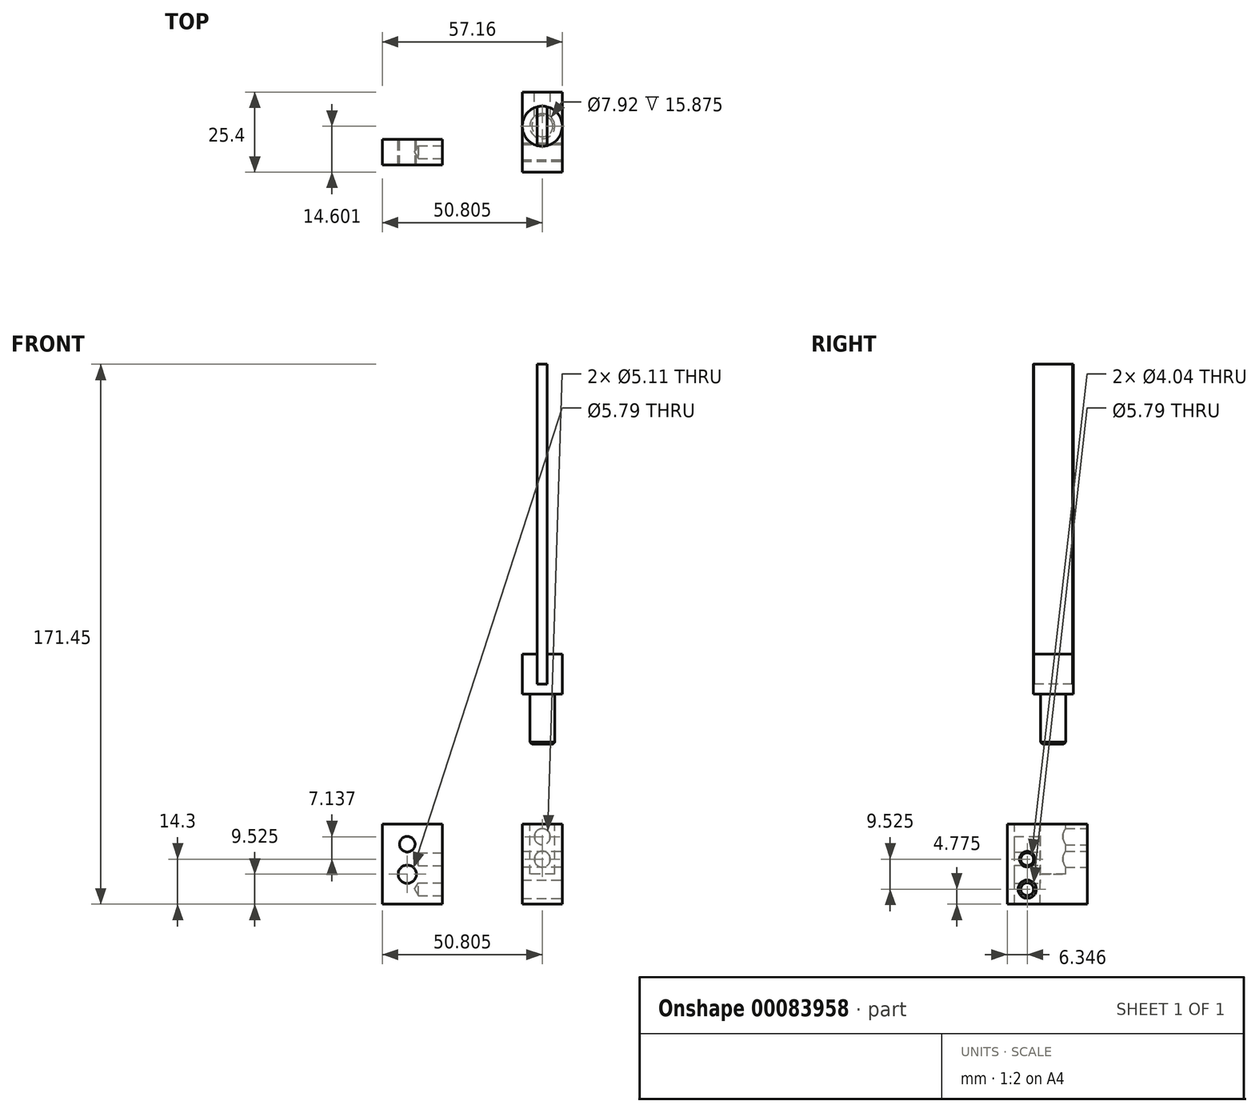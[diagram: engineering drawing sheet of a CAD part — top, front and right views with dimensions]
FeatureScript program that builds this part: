
annotation { "Feature Type Name" : "Feature", "Feature Type Description" : "" }
export const myFeature = defineFeature(function(context is Context, id is Id, definition is map)
    precondition{}
    {
        {
            var Q0;
            Q0=qCreatedBy(makeId("Front.planeOp"),FACE);
            var sketch = newSketch(context, id + "F0", { "sketchPlane" : qUnion([Q0])});
            skLineSegment(sketch, "E0.bottom", {"start": v(-9.52, -12.7) * mm, "end": v(9.53, -12.7) * mm});
            skLineSegment(sketch, "E0.top", {"start": v(-9.53, 12.7) * mm, "end": v(9.53, 12.7) * mm});
            skLineSegment(sketch, "E0.left", {"start": v(-9.53, -12.7) * mm, "end": v(-9.53, 12.7) * mm});
            skLineSegment(sketch, "E0.right", {"start": v(9.53, -12.7) * mm, "end": v(9.53, 12.7) * mm});
            skPoint(sketch, "E0.middle", {"position": v(0, 0) * mm});
            skSolve(sketch);
        }
        {
            var Q0;
            Q0=makeQuery(id+"F0.imprint","IMPRINT",FACE,{"disambiguationData":[TD([[makeQuery(id+"F0.imprint","IMPRINT",EDGE,{"derivedFrom":sQuery(id+"F0.wireOp",EDGE,"E0.bottom")}),1.0]])]});
            extrude(context, id + "F1", {"entities" : qUnion([Q0]), "depth" : 8.13 * mm});
        }
        {
            var Q0;
            Q0=makeQuery(id+"F1.opExtrude","CAP_FACE",FACE,{"disambiguationData":[OSD([sQuery(id+"F0.wireOp",EDGE,"E0.bottom"),sQuery(id+"F0.wireOp",EDGE,"E0.top"),sQuery(id+"F0.wireOp",EDGE,"E0.left"),sQuery(id+"F0.wireOp",EDGE,"E0.right")])],"isStart":true});
            var sketch = newSketch(context, id + "F2", { "sketchPlane" : qUnion([Q0])});
            skLineSegment(sketch, "E1", {"start": v(1.6, 12.7) * mm, "end": v(1.6, -12.7) * mm, "construction": true});
            skLineSegment(sketch, "E2", {"start": v(-9.53, 6.35) * mm, "end": v(9.53, 6.35) * mm, "construction": true});
            skLineSegment(sketch, "E3", {"start": v(-9.53, -3.17) * mm, "end": v(9.53, -3.17) * mm, "construction": true});
            skPoint(sketch, "E4", {"position": v(1.6, 6.35) * mm});
            skPoint(sketch, "E5", {"position": v(1.6, -3.17) * mm});
            skSolve(sketch);
        }
        {
            var Q0;
            Q0=sQuery(id+"F2.wireOp",VERTEX,"E4");
            var Q1;
            Q1=makeQuery(id+"F1.opExtrude","SWEPT_BODY",BODY,{"disambiguationData":[OSD([sQuery(id+"F0.wireOp",EDGE,"E0.bottom"),sQuery(id+"F0.wireOp",EDGE,"E0.top"),sQuery(id+"F0.wireOp",EDGE,"E0.left"),sQuery(id+"F0.wireOp",EDGE,"E0.right")])]});
            hole(context, id + "F3", {"style" : HoleStyle.SIMPLE, "endStyle" : HoleEndStyle.THROUGH, "standardTappedOrClearance" : lookupTablePath({ "standard" : "ANSI", "size" : "#10 (0.2)", "type" : "Drilled" }), "standardBlindInLast" : lookupTablePath({ "standard" : "ANSI", "size" : "#10", "type" : "Drilled" }), "holeDiameter" : 4.9 * mm, "locations" : qUnion([Q0]), "scope" : qUnion([Q1]), "isTappedThrough" : true});
        }
        {
            var Q0;
            Q0=sQuery(id+"F2.wireOp",VERTEX,"E5");
            var Q1;
            Q1=makeQuery(id+"F1.opExtrude","SWEPT_BODY",BODY,{"disambiguationData":[OSD([sQuery(id+"F0.wireOp",EDGE,"E0.bottom"),sQuery(id+"F0.wireOp",EDGE,"E0.top"),sQuery(id+"F0.wireOp",EDGE,"E0.left"),sQuery(id+"F0.wireOp",EDGE,"E0.right")])]});
            hole(context, id + "F4", {"style" : HoleStyle.SIMPLE, "endStyle" : HoleEndStyle.THROUGH, "standardTappedOrClearance" : lookupTablePath({ "standard" : "ANSI", "size" : "#1 (0.23)", "type" : "Drilled" }), "standardBlindInLast" : lookupTablePath({ "standard" : "ANSI", "size" : "#1", "type" : "Drilled" }), "holeDiameter" : 5.8 * mm, "locations" : qUnion([Q0]), "scope" : qUnion([Q1]), "isTappedThrough" : true});
        }
        {
            var Q0;
            Q0=makeQuery(id+"F1.opExtrude","SWEPT_FACE",FACE,{"disambiguationData":[OSD([sQuery(id+"F0.wireOp",EDGE,"E0.right")])]});
            var sketch = newSketch(context, id + "F5", { "sketchPlane" : qUnion([Q0])});
            skLineSegment(sketch, "E6", {"start": v(-4.06, 12.7) * mm, "end": v(-4.06, -12.7) * mm, "construction": true});
            skLineSegment(sketch, "E7", {"start": v(-8.13, 1.6) * mm, "end": v(0, 1.6) * mm, "construction": true});
            skLineSegment(sketch, "E8", {"start": v(-8.13, -7.92) * mm, "end": v(0, -7.92) * mm, "construction": true});
            skPoint(sketch, "E9", {"position": v(-4.06, 1.6) * mm});
            skPoint(sketch, "E10", {"position": v(-4.06, -7.92) * mm});
            skSolve(sketch);
        }
        {
            var Q0;
            Q0=sQuery(id+"F5.wireOp",VERTEX,"E9");
            var Q1;
            Q1=sQuery(id+"F5.wireOp",VERTEX,"E10");
            var Q2;
            Q2=makeQuery(id+"F1.opExtrude","SWEPT_BODY",BODY,{"disambiguationData":[OSD([sQuery(id+"F0.wireOp",EDGE,"E0.bottom"),sQuery(id+"F0.wireOp",EDGE,"E0.top"),sQuery(id+"F0.wireOp",EDGE,"E0.left"),sQuery(id+"F0.wireOp",EDGE,"E0.right")])]});
            hole(context, id + "F6", {"style" : HoleStyle.SIMPLE, "endStyle" : HoleEndStyle.BLIND, "standardTappedOrClearance" : lookupTablePath({ "standard" : "ANSI", "engagement" : "75%", "pitch" : "32 tpi", "size" : "#10", "type" : "Tapped" }), "standardBlindInLast" : lookupTablePath({ "standard" : "ANSI", "engagement" : "75%", "pitch" : "32 tpi", "size" : "#10", "type" : "Tapped" }), "holeDiameter" : 4.04 * mm, "holeDepth" : 7.62 * mm, "locations" : qUnion([Q0, Q1]), "scope" : qUnion([Q2]), "majorDiameter" : 4.83 * mm});
        }
        {
            var Q0;
            Q0=makeQuery(id+"F1.opExtrude","SWEPT_FACE",FACE,{"disambiguationData":[OSD([sQuery(id+"F0.wireOp",EDGE,"E0.right")])]});
            cPlane(context, id + "F7", {"entities" : qUnion([Q0]), "cplaneType" : CPlaneType.OFFSET, "offset" : 25.4 * mm, "width" : 152.4 * mm, "height" : 152.4 * mm});
        }
        {
            var Q0;
            Q0=qCreatedBy(id+"F7.planeOp",FACE);
            var sketch = newSketch(context, id + "F8", { "sketchPlane" : qUnion([Q0])});
            skLineSegment(sketch, "E11.bottom", {"start": v(-10.41, 12.7) * mm, "end": v(14.99, 12.7) * mm});
            skLineSegment(sketch, "E11.top", {"start": v(-10.41, -12.7) * mm, "end": v(14.99, -12.7) * mm});
            skLineSegment(sketch, "E11.left", {"start": v(-10.41, 12.7) * mm, "end": v(-10.41, -12.7) * mm});
            skLineSegment(sketch, "E11.right", {"start": v(14.99, 12.7) * mm, "end": v(14.99, -12.7) * mm});
            skSolve(sketch);
        }
        {
            var Q0;
            Q0=makeQuery(id+"F8.imprint","IMPRINT",FACE,{"disambiguationData":[TD([[makeQuery(id+"F8.imprint","IMPRINT",EDGE,{"derivedFrom":sQuery(id+"F8.wireOp",EDGE,"E11.bottom")}),-1.0]])]});
            extrude(context, id + "F9", {"entities" : qUnion([Q0]), "depth" : 12.7 * mm});
        }
        {
            var Q0;
            Q0=makeQuery(id+"F9.opExtrude","CAP_FACE",FACE,{"disambiguationData":[OSD([sQuery(id+"F8.wireOp",EDGE,"E11.bottom"),sQuery(id+"F8.wireOp",EDGE,"E11.top"),sQuery(id+"F8.wireOp",EDGE,"E11.left"),sQuery(id+"F8.wireOp",EDGE,"E11.right")])],"isStart":false});
            var sketch = newSketch(context, id + "F10", { "sketchPlane" : qUnion([Q0])});
            skPoint(sketch, "E12.0", {"position": v(-4.06, 1.6) * mm});
            skPoint(sketch, "E13.0", {"position": v(-4.06, -7.92) * mm});
            skSolve(sketch);
        }
        {
            var Q0;
            Q0=sQuery(id+"F10.wireOp",VERTEX,"E12.0");
            var Q1;
            Q1=makeQuery(id+"F9.opExtrude","SWEPT_BODY",BODY,{"disambiguationData":[OSD([sQuery(id+"F8.wireOp",EDGE,"E11.bottom"),sQuery(id+"F8.wireOp",EDGE,"E11.top"),sQuery(id+"F8.wireOp",EDGE,"E11.left"),sQuery(id+"F8.wireOp",EDGE,"E11.right")])]});
            hole(context, id + "F11", {"style" : HoleStyle.SIMPLE, "endStyle" : HoleEndStyle.THROUGH, "standardTappedOrClearance" : lookupTablePath({ "standard" : "ANSI", "size" : "#10 (0.2)", "type" : "Drilled" }), "standardBlindInLast" : lookupTablePath({ "standard" : "ANSI", "size" : "#10", "type" : "Drilled" }), "holeDiameter" : 4.9 * mm, "locations" : qUnion([Q0]), "scope" : qUnion([Q1]), "isTappedThrough" : true});
        }
        {
            var Q0;
            Q0=sQuery(id+"F10.wireOp",VERTEX,"E13.0");
            var Q1;
            Q1=makeQuery(id+"F9.opExtrude","SWEPT_BODY",BODY,{"disambiguationData":[OSD([sQuery(id+"F8.wireOp",EDGE,"E11.bottom"),sQuery(id+"F8.wireOp",EDGE,"E11.top"),sQuery(id+"F8.wireOp",EDGE,"E11.left"),sQuery(id+"F8.wireOp",EDGE,"E11.right")])]});
            hole(context, id + "F12", {"style" : HoleStyle.SIMPLE, "endStyle" : HoleEndStyle.THROUGH, "standardTappedOrClearance" : lookupTablePath({ "standard" : "ANSI", "size" : "#1 (0.23)", "type" : "Drilled" }), "standardBlindInLast" : lookupTablePath({ "standard" : "ANSI", "size" : "#1", "type" : "Drilled" }), "holeDiameter" : 5.8 * mm, "locations" : qUnion([Q0]), "scope" : qUnion([Q1]), "isTappedThrough" : true});
        }
        {
            var Q0;
            Q0=makeQuery(id+"F9.opExtrude","SWEPT_FACE",FACE,{"disambiguationData":[OSD([sQuery(id+"F8.wireOp",EDGE,"E11.bottom")])]});
            var sketch = newSketch(context, id + "F13", { "sketchPlane" : qUnion([Q0])});
            skLineSegment(sketch, "E14", {"start": v(41.28, -10.41) * mm, "end": v(41.28, 14.99) * mm, "construction": true});
            skLineSegment(sketch, "E15", {"start": v(34.93, 4.2) * mm, "end": v(47.63, 4.2) * mm, "construction": true});
            skCircle(sketch, "E16", {"center": v(41.28, 4.2) * mm, "radius": 3.96 * mm});
            skSolve(sketch);
        }
        {
            var Q0;
            Q0=makeQuery(id+"F13.imprint","IMPRINT",FACE,{"disambiguationData":[TD([[makeQuery(id+"F13.imprint","IMPRINT",EDGE,{"derivedFrom":sQuery(id+"F13.wireOp",EDGE,"E16")}),1.0]])]});
            extrude(context, id + "F14", {"entities" : qUnion([Q0]), "operationType" : NewBodyOperationType.REMOVE, "oppositeDirection" : true, "depth" : 15.88 * mm});
        }
        {
            var Q0;
            Q0=makeQuery(id+"F9.opExtrude","SWEPT_FACE",FACE,{"disambiguationData":[OSD([sQuery(id+"F8.wireOp",EDGE,"E11.right")])]});
            var sketch = newSketch(context, id + "F15", { "sketchPlane" : qUnion([Q0])});
            skLineSegment(sketch, "E17", {"start": v(-41.28, 12.7) * mm, "end": v(-41.28, -12.7) * mm, "construction": true});
            skLineSegment(sketch, "E18", {"start": v(-47.63, 8.74) * mm, "end": v(-34.93, 8.74) * mm, "construction": true});
            skLineSegment(sketch, "E19", {"start": v(-47.63, 1.6) * mm, "end": v(-34.93, 1.6) * mm, "construction": true});
            skPoint(sketch, "E20", {"position": v(-41.28, 8.74) * mm});
            skPoint(sketch, "E21", {"position": v(-41.28, 1.6) * mm});
            skSolve(sketch);
        }
        {
            var Q0;
            Q0=sQuery(id+"F15.wireOp",VERTEX,"E20");
            var Q1;
            Q1=sQuery(id+"F15.wireOp",VERTEX,"E21");
            var Q2;
            Q2=makeQuery(id+"F9.opExtrude","SWEPT_BODY",BODY,{"disambiguationData":[OSD([sQuery(id+"F8.wireOp",EDGE,"E11.bottom"),sQuery(id+"F8.wireOp",EDGE,"E11.top"),sQuery(id+"F8.wireOp",EDGE,"E11.left"),sQuery(id+"F8.wireOp",EDGE,"E11.right")])]});
            hole(context, id + "F16", {"style" : HoleStyle.SIMPLE, "endStyle" : HoleEndStyle.BLIND, "standardTappedOrClearance" : lookupTablePath({ "standard" : "ANSI", "engagement" : "75%", "pitch" : "20 tpi", "size" : "1/4", "type" : "Tapped" }), "standardBlindInLast" : lookupTablePath({ "standard" : "ANSI", "engagement" : "75%", "pitch" : "20 tpi", "size" : "1/4", "type" : "Tapped" }), "holeDiameter" : 5.1 * mm, "holeDepth" : 7.62 * mm, "locations" : qUnion([Q0, Q1]), "scope" : qUnion([Q2]), "majorDiameter" : 6.35 * mm});
        }
        {
            var Q0;
            Q0=makeQuery(id+"F9.opExtrude","SWEPT_FACE",FACE,{"disambiguationData":[OSD([sQuery(id+"F8.wireOp",EDGE,"E11.bottom")])]});
            cPlane(context, id + "F17", {"entities" : qUnion([Q0]), "cplaneType" : CPlaneType.OFFSET, "offset" : 25.4 * mm, "width" : 152.4 * mm, "height" : 152.4 * mm});
        }
        {
            var Q0;
            Q0=qCreatedBy(id+"F17.planeOp",FACE);
            var sketch = newSketch(context, id + "F18", { "sketchPlane" : qUnion([Q0])});
            skCircle(sketch, "E22.0", {"center": v(41.28, 4.2) * mm, "radius": 3.96 * mm, "construction": true});
            skCircle(sketch, "E23", {"center": v(41.28, 4.2) * mm, "radius": 3.96 * mm});
            skSolve(sketch);
        }
        {
            var Q0;
            Q0=makeQuery(id+"F18.imprint","IMPRINT",FACE,{"disambiguationData":[TD([[makeQuery(id+"F18.imprint","IMPRINT",EDGE,{"derivedFrom":sQuery(id+"F18.wireOp",EDGE,"E23")}),1.0]])]});
            extrude(context, id + "F19", {"entities" : qUnion([Q0]), "depth" : 15.88 * mm});
        }
        {
            var Q0;
            Q0=makeQuery(id+"F19.opExtrude","CAP_FACE",FACE,{"disambiguationData":[OSD([sQuery(id+"F18.wireOp",EDGE,"E23")])],"isStart":false});
            var sketch = newSketch(context, id + "F20", { "sketchPlane" : qUnion([Q0])});
            skCircle(sketch, "E24", {"center": v(41.28, 4.2) * mm, "radius": 6.35 * mm});
            skSolve(sketch);
        }
        {
            var Q0;
            Q0=makeQuery(id+"F20.imprint","IMPRINT",FACE,{"disambiguationData":[TD([[makeQuery(id+"F20.imprint","IMPRINT",EDGE,{"derivedFrom":sQuery(id+"F20.wireOp",EDGE,"E24")}),1.0]])]});
            var Q1;
            Q1=makeQuery(id+"F20.imprint","IMPRINT",FACE,{"disambiguationData":[TD([[makeQuery(id+"F20.imprint","IMPRINT",EDGE,{"derivedFrom":makeQuery(id+"F19.opExtrude","CAP_EDGE",EDGE,{"disambiguationData":[OSD([sQuery(id+"F18.wireOp",EDGE,"E23")])],"isStart":false})}),1.0]])]});
            extrude(context, id + "F21", {"entities" : qUnion([Q0, Q1]), "operationType" : NewBodyOperationType.ADD, "depth" : 12.7 * mm});
        }
        {
            var Q0;
            Q0=makeQuery(id+"F21.opExtrude","CAP_FACE",FACE,{"disambiguationData":[OSD([sQuery(id+"F20.wireOp",EDGE,"E24")])],"isStart":false});
            var sketch = newSketch(context, id + "F22", { "sketchPlane" : qUnion([Q0])});
            skCircle(sketch, "E25.0", {"center": v(41.27, 4.2) * mm, "radius": 6.35 * mm});
            skLineSegment(sketch, "E26", {"start": v(39.69, 10.34) * mm, "end": v(39.69, -1.96) * mm});
            skLineSegment(sketch, "E27", {"start": v(42.86, 10.34) * mm, "end": v(42.86, -1.96) * mm});
            skSolve(sketch);
        }
        {
            var Q0;
            {var subQ0=sQuery(id+"F22.wireOp",EDGE,"E26");Q0=makeQuery(id+"F22.imprint","IMPRINT",FACE,{"disambiguationData":[TD([[makeQuery(id+"F22.imprint","IMPRINT",EDGE,{"derivedFrom":subQ0}),1.0]])]});}
            extrude(context, id + "F23", {"entities" : qUnion([Q0]), "operationType" : NewBodyOperationType.REMOVE, "oppositeDirection" : true, "depth" : 9.52 * mm});
        }
        {
            var Q0;
            Q0=makeQuery(id+"F23.boolean.opBoolean","COPY",FACE,{"derivedFrom":makeQuery(id+"F23.opExtrude","CAP_FACE",FACE,{"disambiguationData":[OSD([sQuery(id+"F22.wireOp",EDGE,"E25.0"),sQuery(id+"F22.wireOp",EDGE,"E26"),sQuery(id+"F22.wireOp",EDGE,"E27")])],"isStart":false})});
            extrude(context, id + "F24", {"entities" : qUnion([Q0]), "depth" : 101.6 * mm});
        }
        {
            var Q0;
            Q0=makeQuery(id+"F19.opExtrude","CAP_EDGE",EDGE,{"disambiguationData":[OSD([sQuery(id+"F18.wireOp",EDGE,"E23")])],"isStart":true});
            chamfer(context, id + "F25", {"entities" : qUnion([Q0]), "width" : 0.64 * mm, "tangentPropagation" : true});
        }
    });
